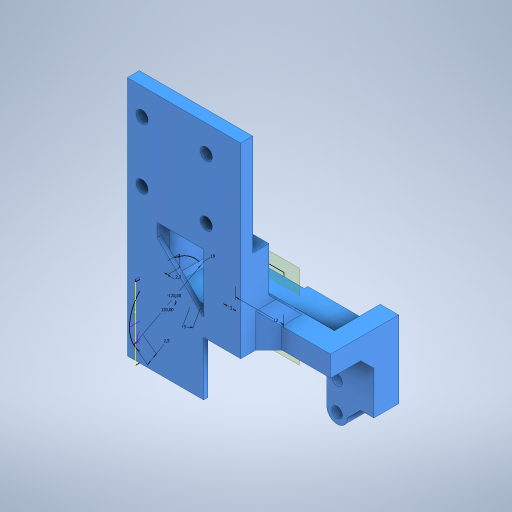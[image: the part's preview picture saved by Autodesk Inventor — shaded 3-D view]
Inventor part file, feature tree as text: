
AUTODESK INVENTOR PART (.ipt)
format: ipt  version: 2024.2 (Build 282272000, 272)  size: 780,288 bytes
history: native  units: mm
features: chamfer x28, extrude x26, sketch x26, other x11, projected_geometry x4, reference x1
ambient origin geometry x8: Origin, YZ Plane, XZ Plane, XY Plane, X Axis, Y Axis, Z Axis, Center Point
bodies: Body1 (feature_tree)
feature tree (96):
  other  "Твердое тело1"
  extrude  "Выдавливание1"  Depth=8.0mm
  sketch  "Эскиз2"
  sketch  "Эскиз3"
  extrude  "Выдавливание3"  Depth=6.0mm TaperAngle=0.0deg
  extrude  "Выдавливание4"  Depth=4.0mm
  extrude  "Выдавливание2"  Depth=4.0mm
  other  "РабПлоскость2"
  sketch  "Эскиз5"
  extrude  "Выдавливание5"  Depth=10.0mm
  other  "РабПлоскость4"
  other  "РабПлоскость5"
  extrude  "Выдавливание14"  Depth=2.0mm
  other  "РабПлоскость6"
  sketch  "Эскиз17"
  extrude  "Выдавливание15"  Depth=8.0mm
  chamfer  "Фаска6"  Distance=12.0mm
  extrude  "Выдавливание16"  Depth=2.0mm
  chamfer  "Фаска7"  Distance=2.0mm
  extrude  "Выдавливание17"  Depth=1.0mm
  extrude  "Выдавливание18"  Depth=1.0mm
  chamfer  "Фаска8"  Distance=2.0mm
  sketch  "Эскиз23"
  other  "РабПлоскость7"
  chamfer  "Фаска3"  [1 undecoded]
  extrude  "Выдавливание21"  Depth=12.0mm
  extrude  "Выдавливание23"  Depth=8.0mm
  extrude  "Выдавливание24"  Depth=3.0mm
  extrude  "Выдавливание25"  Depth=19.0mm
  chamfer  "Фаска16"  Distance=2.2mm
  extrude  "Выдавливание26"  Depth=3.0mm
  chamfer  "Фаска17"  Distance=3.0mm
  chamfer  "Фаска18"  Distance=3.0mm
  chamfer  "Фаска20"  Distance=9.0mm
  sketch  "Эскиз31"
  extrude  "Выдавливание27"  Depth=10.0mm TaperAngle=0.0deg
  extrude  "Выдавливание28"  Depth=1.0mm
  chamfer  "Фаска21"  Distance=1.0mm
  chamfer  "Фаска22"  Distance=13.0mm
  chamfer  "Фаска23"  Distance=10.0mm
  extrude  "Выдавливание29"  Depth=5.0mm TaperAngle=45.0deg
  extrude  "Выдавливание30"  Depth=12.0mm
  extrude  "Выдавливание31"  Depth=3.0mm
  chamfer  "Фаска24"  Distance=13.0mm
  chamfer  "Фаска25"  Distance=10.0mm
  extrude  "Выдавливание32"  Depth=10.0mm TaperAngle=0.0deg
  chamfer  "Фаска26"  Distance=18.0mm Angle=45.0deg
  sketch  "Эскиз37"
  chamfer  "Фаска27"  Distance=14.0mm
  chamfer  "Фаска28"  Distance=5.6mm
  chamfer  "Фаска29"  Distance=13.0mm
  chamfer  "Фаска30"  Distance=2.0mm Angle=45.0deg
  chamfer  "Фаска31"  Distance=5.5mm
  chamfer  "Фаска32"  Distance=7.0mm
  extrude  "Выдавливание33"  TaperAngle=0.0deg  [1 undecoded]
  chamfer  "Фаска33"  Distance=5.0mm
  extrude  "Выдавливание34"  Depth=2.0mm TaperAngle=45.0deg
  chamfer  "Фаска34"  Distance=3.029555mm
  chamfer  "Фаска35"  Distance=18.0mm
  extrude  "Выдавливание35"  Depth=2.5mm
  chamfer  "Фаска36"  Distance=2.5mm
  chamfer  "Фаска37"  Distance=7.0mm
  chamfer  "Фаска38"  Distance=6.173mm
  chamfer  "Фаска39"  Distance=2.25mm
  sketch  "Эскиз41"
  extrude  "Выдавливание36"  Depth=2.25mm
  extrude  "Выдавливание37"  Depth=19.0mm
  chamfer  "Фаска40"  Distance=2.4mm
  sketch  "Эскиз1"
  projected_geometry  "Спроецированная петля1"
  sketch  "Эскиз4"
  other  "РабПлоскость1"
  sketch  "Эскиз16"
  sketch  "Эскиз18"
  sketch  "Эскиз19"
  sketch  "Эскиз25"
  sketch  "Эскиз27"
  sketch  "Эскиз28"
  projected_geometry  "Спроецированная петля6"
  projected_geometry  "Спроецированная петля7"
  sketch  "Эскиз29"
  projected_geometry  "Спроецированная петля8"
  sketch  "Эскиз30"
  reference  "Ссылка10"
  sketch  "Эскиз32"
  sketch  "Эскиз33"
  sketch  "Эскиз34"
  sketch  "Эскиз35"
  sketch  "Эскиз36"
  sketch  "Эскиз38"
  sketch  "Эскиз39"
  sketch  "Эскиз40"
  other  "<userpath>\Documents\Artist-v2\3D\каретка.iam"
  other  "каретка.iam"
  other  "Сервопривод:1"
  other  "Проецирование ребер1"
note: 2 required parameter values undecoded (feature->parameter linkage not recoverable at this tier; creation-order binding heuristic only, values carry confidence <= 0.55)
